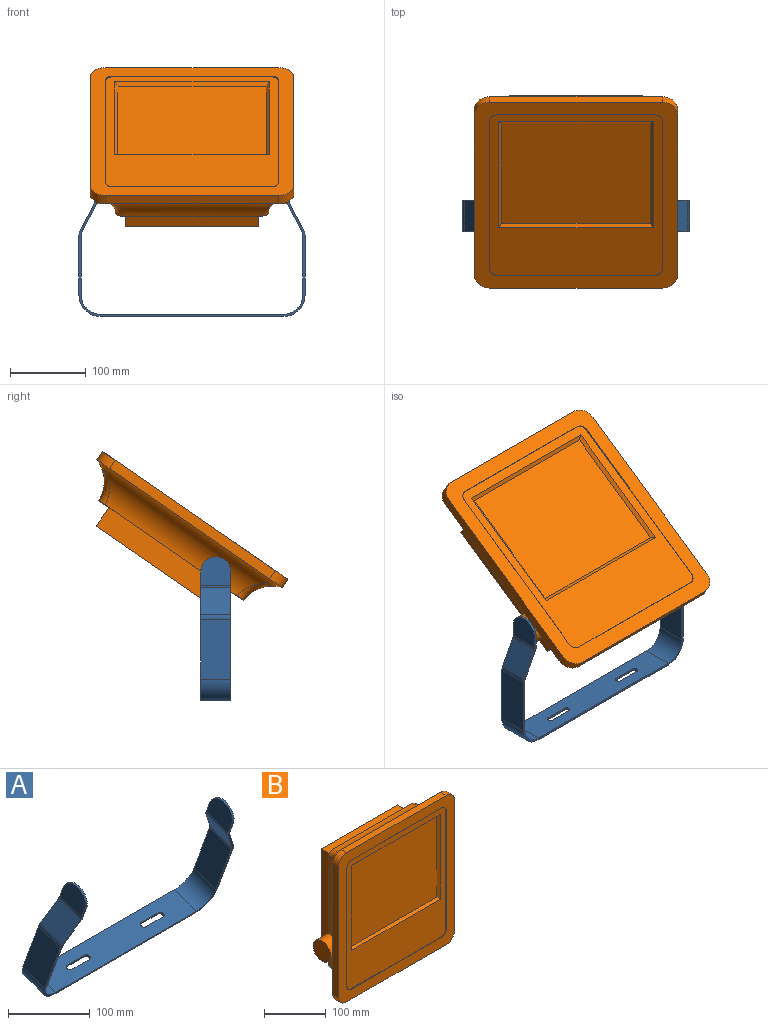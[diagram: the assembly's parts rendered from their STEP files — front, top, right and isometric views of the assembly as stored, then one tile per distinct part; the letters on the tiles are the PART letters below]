
ASSEMBLY  parts=2 mates=1
PART A: 38 faces, bbox 298x96.7x186 mm
  f0: plane 30x2.82mm, normal (0,0.94,0.34), area 90mm2, adj f1,f3,f20,f32
  f1: cylinder r=4mm len=8.54mm, axis (0,-0.34,0.94), area 37.7mm2, adj f0,f2,f20,f32
  f2: plane 30x2.82mm, normal (0,-0.94,-0.34), area 90mm2, adj f1,f3,f20,f32
  f3: cylinder r=4mm len=8.54mm, axis (0,-0.34,0.94), area 37.7mm2, adj f0,f2,f20,f32
  f4: plane 30x2.82mm, normal (0,-0.94,-0.34), area 90mm2, adj f5,f7,f20,f32
  f5: cylinder r=4mm len=8.54mm, axis (0,-0.34,0.94), area 37.7mm2, adj f4,f6,f20,f32
  f6: plane 30x2.82mm, normal (0,0.94,0.34), area 90mm2, adj f5,f7,f20,f32
  f7: cylinder r=4mm len=8.54mm, axis (0,-0.34,0.94), area 37.7mm2, adj f4,f6,f20,f32
  f8: plane 44.79x43.32mm, normal (-1,0,0), area 1329.7mm2, adj f9,f10,f13,f37
  f9: cylinder r=20mm len=38.79mm, axis (1,0,0), area 188.5mm2, adj f8,f10,f14,f37
  f10: plane 297.98x159.11mm, normal (0,0.94,0.34), area 1853.5mm2, adj f8,f9,f11,f12,f13,f14,f15,f16
  f11: plane 44.79x43.32mm, normal (-1,0,0), area 1329.7mm2, adj f10,f12,f25,f37
  f12: cylinder r=20mm len=38.79mm, axis (1,0,0), area 188.5mm2, adj f10,f11,f26,f37
  f13: cylinder r=7mm len=38.7mm, axis (0,-0.94,-0.34), area 135.3mm2, adj f8,f10,f36,f37
  f14: plane 44.79x43.32mm, normal (1,0,0), area 1329.7mm2, adj f9,f10,f15,f37
  f15: cylinder r=10mm len=39.18mm, axis (0,-0.94,-0.34), area 193.3mm2, adj f10,f14,f16,f37
  f16: plane 49.78x47.17mm, normal (0.89,0.16,-0.44), area 1609.8mm2, adj f10,f15,f17,f37
  f17: cylinder r=10mm len=39.18mm, axis (0,-0.94,-0.34), area 193.3mm2, adj f10,f16,f18,f37
  f18: plane 87.78x64.56mm, normal (1,0,0), area 3154.3mm2, adj f10,f17,f19,f37
  f19: cylinder r=25mm len=46.14mm, axis (0,-0.94,-0.34), area 1570.8mm2, adj f10,f18,f20,f37
  f20: plane 241.98x37.59mm, normal (0,-0.34,0.94), area 9098.8mm2, adj f0,f1,f2,f3,f4,f5,f6,f7
  f21: cylinder r=25mm len=46.14mm, axis (0,-0.94,-0.34), area 1570.8mm2, adj f10,f20,f22,f37
  f22: plane 87.78x64.56mm, normal (-1,0,0), area 3154.3mm2, adj f10,f21,f23,f37
  f23: cylinder r=10mm len=39.18mm, axis (0,-0.94,-0.34), area 193.3mm2, adj f10,f22,f24,f37
  f24: plane 49.78x47.17mm, normal (-0.89,0.16,-0.44), area 1609.8mm2, adj f10,f23,f25,f37
  f25: cylinder r=10mm len=39.18mm, axis (0,-0.94,-0.34), area 193.3mm2, adj f10,f11,f24,f37
  f26: plane 44.79x43.32mm, normal (1,0,0), area 1329.7mm2, adj f10,f12,f27,f37
  f27: cylinder r=7mm len=38.7mm, axis (0,-0.94,-0.34), area 135.3mm2, adj f10,f26,f28,f37
  f28: plane 49.78x47.17mm, normal (0.89,-0.16,0.44), area 1609.8mm2, adj f10,f27,f29,f37
  f29: cylinder r=13mm len=39.65mm, axis (0,-0.94,-0.34), area 251.3mm2, adj f10,f28,f30,f37
  f30: plane 87.78x64.56mm, normal (1,0,0), area 3154.3mm2, adj f10,f29,f31,f37
  f31: cylinder r=28mm len=47.16mm, axis (0,-0.94,-0.34), area 1759.3mm2, adj f10,f30,f32,f37
  f32: plane 241.98x37.59mm, normal (0,0.34,-0.94), area 9098.8mm2, adj f0,f1,f2,f3,f4,f5,f6,f7
  f33: cylinder r=28mm len=47.16mm, axis (0,-0.94,-0.34), area 1759.3mm2, adj f10,f32,f34,f37
  f34: plane 87.78x64.56mm, normal (-1,0,0), area 3154.3mm2, adj f10,f33,f35,f37
  f35: cylinder r=13mm len=39.65mm, axis (0,-0.94,-0.34), area 251.3mm2, adj f10,f34,f36,f37
  f36: plane 49.78x47.17mm, normal (-0.89,-0.16,0.44), area 1609.8mm2, adj f10,f13,f35,f37
  f37: plane 297.98x159.11mm, normal (0,-0.94,-0.34), area 1853.5mm2, adj f8,f9,f11,f12,f13,f14,f15,f16
PART B: 46 faces, bbox 268.5x111.9x297.5 mm
  f0: cylinder r=20mm len=40mm, axis (-1,0,0), area 3096mm2, adj f3,f5,f6,f9,f14
  f1: cylinder r=20mm len=40mm, axis (-1,0,0), area 3074.7mm2, adj f2,f4,f6,f7,f14
  f2: plane 40x40mm, normal (1,0,0), area 1256.6mm2, adj f1
  f3: plane 40x40mm, normal (-1,0,0), area 1256.6mm2, adj f0
  f4: cylinder r=48.79mm len=257mm, axis (0,0,-1), area 12728.8mm2, adj f1,f6,f14,f15,f18,f19,f22,f43
  f5: cylinder r=48.79mm len=257mm, axis (0,0,1), area 12728.8mm2, adj f0,f6,f12,f14,f16,f17,f21,f25
  f6: plane 202.72x163.53mm, normal (0,1,0), area 7121.3mm2, adj f0,f1,f4,f5,f7,f8,f9,f16
  f7: plane 196.09x30mm, normal (1,0,0), area 5619.5mm2, adj f1,f6,f8,f10,f11,f14
  f8: plane 175.45x30mm, normal (0,0,1), area 5263.6mm2, adj f6,f7,f9,f11
  f9: plane 196.09x30mm, normal (-1,0,0), area 5619.5mm2, adj f0,f6,f8,f10,f11,f14
  f10: plane 175.45x30mm, normal (0,0,-1), area 5263.6mm2, adj f7,f9,f11,f14
  f11: plane 196.09x175.45mm, normal (0,1,0), area 34404.4mm2, adj f7,f8,f9,f10
  f12: bspline ~36.22x29.46mm, area 600.9mm2, adj f5,f13,f14,f21
  f13: cylinder r=48.79mm len=228mm, axis (-1,0,0), area 12136.5mm2, adj f12,f14,f15,f21,f22,f41
  f14: plane 202.72x33.53mm, normal (0,1,0), area 4189.3mm2, adj f0,f1,f4,f5,f7,f9,f10,f12
  f15: bspline ~36.22x29.46mm, area 600.9mm2, adj f4,f13,f14,f22
  f16: bspline ~35.81x28.97mm, area 600.9mm2, adj f5,f6,f17,f20
  f17: torus R=35.78mm, axis (0,1,0), area 324.6mm2, adj f5,f16,f20,f24
  f18: bspline ~36.22x29.46mm, area 600.9mm2, adj f4,f6,f19,f20
  f19: torus R=35.78mm, axis (0,1,0), area 324.6mm2, adj f4,f18,f20,f44
  f20: cylinder r=48.79mm len=228mm, axis (1,0,0), area 12136.5mm2, adj f6,f16,f17,f18,f19,f23
  f21: torus R=35.78mm, axis (0,1,0), area 324.6mm2, adj f5,f12,f13,f26
  f22: torus R=35.78mm, axis (0,1,0), area 324.6mm2, adj f4,f13,f15,f42
  f23: plane 228x13mm, normal (0,0,1), area 2964mm2, adj f20,f24,f44,f45
  f24: cylinder r=20mm len=20mm, axis (0,1,0), area 408.4mm2, adj f17,f23,f25,f45
  f25: plane 257x13mm, normal (-1,0,0), area 3341mm2, adj f5,f24,f26,f45
  f26: cylinder r=20mm len=20mm, axis (0,1,0), area 408.4mm2, adj f21,f25,f41,f45
  f27: plane 169x4mm, normal (-0.71,-0.71,0), area 933.4mm2, adj f28,f30,f31,f40
  f28: plane 204x4mm, normal (0,-0.71,0.71), area 1131.4mm2, adj f27,f29,f31,f40
  f29: plane 169x4mm, normal (0.71,-0.71,0), area 933.4mm2, adj f28,f30,f31,f40
  f30: plane 204x4mm, normal (0,-0.71,-0.71), area 1131.4mm2, adj f27,f29,f31,f40
  f31: plane 196x161mm, normal (0,-1,0), area 31556mm2, adj f27,f28,f29,f30
  f32: plane 237x1mm, normal (1,0,0), area 237mm2, adj f33,f39,f40,f45
  f33: cylinder r=10mm len=10mm, axis (0,1,0), area 15.7mm2, adj f32,f34,f40,f45
  f34: plane 208x1mm, normal (0,0,1), area 208mm2, adj f33,f35,f40,f45
  f35: cylinder r=10mm len=10mm, axis (0,1,0), area 15.7mm2, adj f34,f36,f40,f45
  f36: plane 237x1mm, normal (-1,0,0), area 237mm2, adj f35,f37,f40,f45
  f37: cylinder r=10mm len=10mm, axis (0,1,0), area 15.7mm2, adj f36,f38,f40,f45
  f38: plane 208x1mm, normal (0,0,-1), area 208mm2, adj f37,f39,f40,f45
  f39: cylinder r=10mm len=10mm, axis (0,1,0), area 15.7mm2, adj f32,f38,f40,f45
  f40: plane 257x228mm, normal (0,-1,0), area 24034.2mm2, adj f27,f28,f29,f30,f32,f33,f34,f35
  f41: plane 228x13mm, normal (0,0,-1), area 2964mm2, adj f13,f26,f42,f45
  f42: cylinder r=20mm len=20mm, axis (0,1,0), area 408.4mm2, adj f22,f41,f43,f45
  f43: plane 257x13mm, normal (1,0,0), area 3341mm2, adj f4,f42,f44,f45
  f44: cylinder r=20mm len=20mm, axis (0,1,0), area 408.4mm2, adj f19,f23,f43,f45
  f45: plane 297x268mm, normal (0,-1,0), area 20742.5mm2, adj f23,f24,f25,f26,f32,f33,f34,f35
PLACE A rot(axis=(-1,0,0),20deg) t=(-3877.48,537.59,1782.32)mm
PLACE B rot(axis=(-1,0,0),55.4deg) t=(-3877.48,1372.39,1172.35)mm
MATE revolute B.f0 <-> A.f11  axis (1,0,0) through (125,-0.01,168.71)mm
